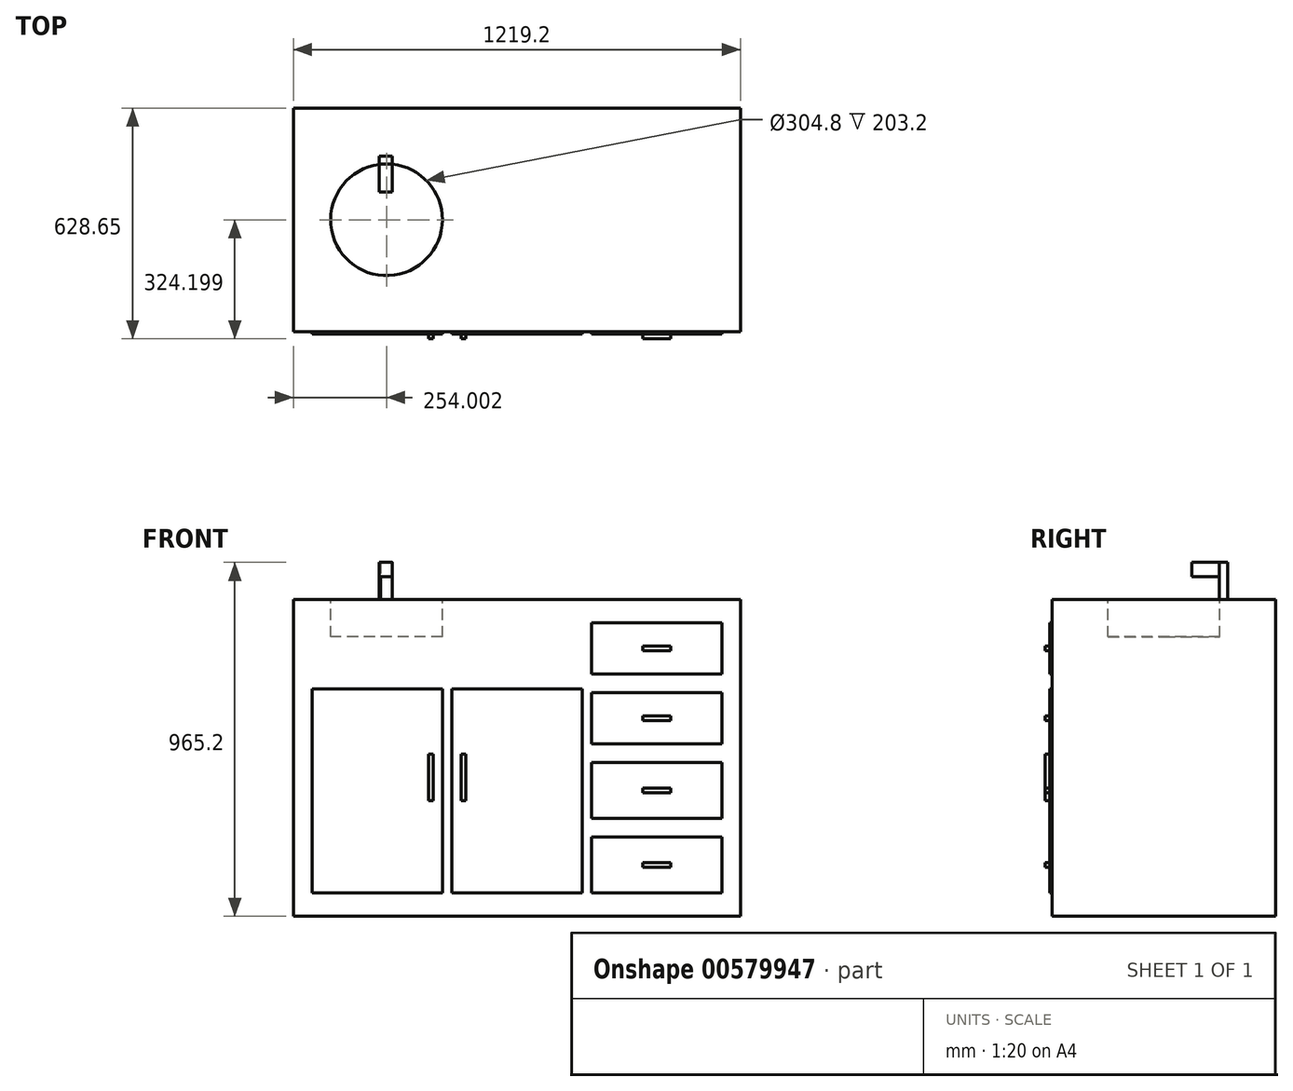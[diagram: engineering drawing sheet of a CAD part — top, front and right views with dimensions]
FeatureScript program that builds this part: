
annotation { "Feature Type Name" : "Feature", "Feature Type Description" : "" }
export const myFeature = defineFeature(function(context is Context, id is Id, definition is map)
    precondition{}
    {
        {
            var Q0;
            Q0=qCreatedBy(makeId("Top.planeOp"),FACE);
            var sketch = newSketch(context, id + "F0", { "sketchPlane" : qUnion([Q0])});
            skLineSegment(sketch, "E0.bottom", {"start": v(-528.54, 334.5) * mm, "end": v(690.66, 334.5) * mm});
            skLineSegment(sketch, "E0.top", {"start": v(-528.54, -275.1) * mm, "end": v(690.66, -275.1) * mm});
            skLineSegment(sketch, "E0.left", {"start": v(-528.54, 334.5) * mm, "end": v(-528.54, -275.1) * mm});
            skLineSegment(sketch, "E0.right", {"start": v(690.66, 334.5) * mm, "end": v(690.66, -275.1) * mm});
            skSolve(sketch);
        }
        {
            var Q0;
            Q0=makeQuery(id+"F0.imprint","IMPRINT",FACE,{"disambiguationData":[TD([[makeQuery(id+"F0.imprint","IMPRINT",EDGE,{"derivedFrom":sQuery(id+"F0.wireOp",EDGE,"E0.bottom")}),-1.0]])]});
            extrude(context, id + "F1", {"entities" : qUnion([Q0]), "depth" : 863.6 * mm, "offsetDistance" : 25.4 * mm});
        }
        {
            var Q0;
            Q0=makeQuery(id+"F1.opExtrude","SWEPT_FACE",FACE,{"disambiguationData":[OSD([sQuery(id+"F0.wireOp",EDGE,"E0.top")])]});
            var sketch = newSketch(context, id + "F2", { "sketchPlane" : qUnion([Q0])});
            skLineSegment(sketch, "E1.bottom", {"start": v(-477.74, 620.01) * mm, "end": v(-122.14, 620.01) * mm});
            skLineSegment(sketch, "E1.top", {"start": v(-477.74, 63.5) * mm, "end": v(-122.14, 63.5) * mm});
            skLineSegment(sketch, "E1.left", {"start": v(-477.74, 620.01) * mm, "end": v(-477.74, 63.5) * mm});
            skLineSegment(sketch, "E1.right", {"start": v(-96.74, 620.01) * mm, "end": v(-96.74, 63.5) * mm});
            skLineSegment(sketch, "E2.bottom", {"start": v(-96.74, 620.01) * mm, "end": v(258.86, 620.01) * mm});
            skLineSegment(sketch, "E2.top", {"start": v(-96.74, 63.5) * mm, "end": v(258.86, 63.5) * mm});
            skLineSegment(sketch, "E2.left", {"start": v(-122.14, 620.01) * mm, "end": v(-122.14, 63.5) * mm});
            skLineSegment(sketch, "E2.right", {"start": v(258.86, 620.01) * mm, "end": v(258.86, 63.5) * mm});
            skLineSegment(sketch, "E3.bottom", {"start": v(284.26, 609.6) * mm, "end": v(639.86, 609.6) * mm});
            skLineSegment(sketch, "E3.top", {"start": v(284.26, 469.9) * mm, "end": v(639.86, 469.9) * mm});
            skLineSegment(sketch, "E3.left", {"start": v(284.26, 609.6) * mm, "end": v(284.26, 469.9) * mm});
            skLineSegment(sketch, "E3.right", {"start": v(639.86, 609.6) * mm, "end": v(639.86, 469.9) * mm});
            skLineSegment(sketch, "E4.bottom", {"start": v(284.26, 419.1) * mm, "end": v(639.86, 419.1) * mm});
            skLineSegment(sketch, "E4.top", {"start": v(284.26, 266.7) * mm, "end": v(639.86, 266.7) * mm});
            skLineSegment(sketch, "E4.left", {"start": v(284.26, 419.1) * mm, "end": v(284.26, 266.7) * mm});
            skLineSegment(sketch, "E4.right", {"start": v(639.86, 419.1) * mm, "end": v(639.86, 266.7) * mm});
            skLineSegment(sketch, "E5.bottom", {"start": v(284.26, 63.5) * mm, "end": v(639.86, 63.5) * mm});
            skLineSegment(sketch, "E5.top", {"start": v(284.26, 215.9) * mm, "end": v(639.86, 215.9) * mm});
            skLineSegment(sketch, "E5.left", {"start": v(284.26, 63.5) * mm, "end": v(284.26, 215.9) * mm});
            skLineSegment(sketch, "E5.right", {"start": v(639.86, 63.5) * mm, "end": v(639.86, 215.9) * mm});
            skLineSegment(sketch, "E6.bottom", {"start": v(284.26, 800.1) * mm, "end": v(639.86, 800.1) * mm});
            skLineSegment(sketch, "E6.top", {"start": v(284.26, 660.4) * mm, "end": v(639.86, 660.4) * mm});
            skLineSegment(sketch, "E6.left", {"start": v(284.26, 800.1) * mm, "end": v(284.26, 660.4) * mm});
            skLineSegment(sketch, "E6.right", {"start": v(639.86, 800.1) * mm, "end": v(639.86, 660.4) * mm});
            skSolve(sketch);
        }
        {
            var Q0;
            Q0 = qSketchRegion(id + "F2", true);
            extrude(context, id + "F3", {"entities" : qUnion([Q0]), "operationType" : NewBodyOperationType.ADD, "depth" : 6.35 * mm, "offsetDistance" : 25.4 * mm});
        }
        {
            var Q0;
            Q0=makeQuery(id+"F3.opExtrude","CAP_FACE",FACE,{"disambiguationData":[OSD([sQuery(id+"F2.wireOp",EDGE,"E1.bottom"),sQuery(id+"F2.wireOp",EDGE,"E1.top"),sQuery(id+"F2.wireOp",EDGE,"E1.left"),sQuery(id+"F2.wireOp",EDGE,"E2.left")])],"isStart":false});
            var sketch = newSketch(context, id + "F4", { "sketchPlane" : qUnion([Q0])});
            skLineSegment(sketch, "E7.bottom", {"start": v(-160.24, 442.21) * mm, "end": v(-147.54, 442.21) * mm});
            skLineSegment(sketch, "E7.top", {"start": v(-160.24, 315.21) * mm, "end": v(-147.54, 315.21) * mm});
            skLineSegment(sketch, "E7.left", {"start": v(-160.24, 442.21) * mm, "end": v(-160.24, 315.21) * mm});
            skLineSegment(sketch, "E7.right", {"start": v(-147.54, 442.21) * mm, "end": v(-147.54, 315.21) * mm});
            skLineSegment(sketch, "E8.bottom", {"start": v(-71.34, 442.21) * mm, "end": v(-58.64, 442.21) * mm});
            skLineSegment(sketch, "E8.top", {"start": v(-71.34, 315.21) * mm, "end": v(-58.64, 315.21) * mm});
            skLineSegment(sketch, "E8.left", {"start": v(-71.34, 442.21) * mm, "end": v(-71.34, 315.21) * mm});
            skLineSegment(sketch, "E8.right", {"start": v(-58.64, 442.21) * mm, "end": v(-58.64, 315.21) * mm});
            skLineSegment(sketch, "E9.bottom", {"start": v(423.96, 736.6) * mm, "end": v(500.16, 736.6) * mm});
            skLineSegment(sketch, "E9.top", {"start": v(423.96, 723.9) * mm, "end": v(500.16, 723.9) * mm});
            skLineSegment(sketch, "E9.left", {"start": v(423.96, 736.6) * mm, "end": v(423.96, 723.9) * mm});
            skLineSegment(sketch, "E9.right", {"start": v(500.16, 736.6) * mm, "end": v(500.16, 723.9) * mm});
            skLineSegment(sketch, "E10.bottom", {"start": v(423.96, 546.1) * mm, "end": v(500.16, 546.1) * mm});
            skLineSegment(sketch, "E10.top", {"start": v(423.96, 533.4) * mm, "end": v(500.16, 533.4) * mm});
            skLineSegment(sketch, "E10.left", {"start": v(423.96, 546.1) * mm, "end": v(423.96, 533.4) * mm});
            skLineSegment(sketch, "E10.right", {"start": v(500.16, 546.1) * mm, "end": v(500.16, 533.4) * mm});
            skLineSegment(sketch, "E11.bottom", {"start": v(423.96, 349.25) * mm, "end": v(500.16, 349.25) * mm});
            skLineSegment(sketch, "E11.top", {"start": v(423.96, 336.55) * mm, "end": v(500.16, 336.55) * mm});
            skLineSegment(sketch, "E11.left", {"start": v(423.96, 349.25) * mm, "end": v(423.96, 336.55) * mm});
            skLineSegment(sketch, "E11.right", {"start": v(500.16, 349.25) * mm, "end": v(500.16, 336.55) * mm});
            skLineSegment(sketch, "E12.bottom", {"start": v(423.96, 146.05) * mm, "end": v(500.16, 146.05) * mm});
            skLineSegment(sketch, "E12.top", {"start": v(423.96, 133.35) * mm, "end": v(500.16, 133.35) * mm});
            skLineSegment(sketch, "E12.left", {"start": v(423.96, 146.05) * mm, "end": v(423.96, 133.35) * mm});
            skLineSegment(sketch, "E12.right", {"start": v(500.16, 146.05) * mm, "end": v(500.16, 133.35) * mm});
            skSolve(sketch);
        }
        {
            var Q0;
            Q0 = qSketchRegion(id + "F4", true);
            extrude(context, id + "F5", {"entities" : qUnion([Q0]), "operationType" : NewBodyOperationType.ADD, "depth" : 12.7 * mm, "offsetDistance" : 25.4 * mm});
        }
        {
            var Q0;
            Q0=makeQuery(id+"F1.opExtrude","CAP_FACE",FACE,{"disambiguationData":[OSD([sQuery(id+"F0.wireOp",EDGE,"E0.bottom"),sQuery(id+"F0.wireOp",EDGE,"E0.top"),sQuery(id+"F0.wireOp",EDGE,"E0.left"),sQuery(id+"F0.wireOp",EDGE,"E0.right")])],"isStart":false});
            var sketch = newSketch(context, id + "F6", { "sketchPlane" : qUnion([Q0])});
            skCircle(sketch, "E13", {"center": v(-274.54, 30.05) * mm, "radius": 152.4 * mm});
            skSolve(sketch);
        }
        {
            var Q0;
            Q0=makeQuery(id+"F6.imprint","IMPRINT",FACE,{"disambiguationData":[TD([[makeQuery(id+"F6.imprint","IMPRINT",EDGE,{"derivedFrom":sQuery(id+"F6.wireOp",EDGE,"E13")}),1.0]])]});
            extrude(context, id + "F7", {"entities" : qUnion([Q0]), "operationType" : NewBodyOperationType.REMOVE, "oppositeDirection" : true, "depth" : 101.6 * mm, "offsetDistance" : 25.4 * mm});
        }
        {
            var Q0;
            Q0=makeQuery(id+"F1.opExtrude","CAP_FACE",FACE,{"disambiguationData":[OSD([sQuery(id+"F0.wireOp",EDGE,"E0.bottom"),sQuery(id+"F0.wireOp",EDGE,"E0.top"),sQuery(id+"F0.wireOp",EDGE,"E0.left"),sQuery(id+"F0.wireOp",EDGE,"E0.right")])],"isStart":false});
            var sketch = newSketch(context, id + "F8", { "sketchPlane" : qUnion([Q0])});
            skLineSegment(sketch, "E14.bottom", {"start": v(-295.12, 203.31) * mm, "end": v(-258.59, 203.31) * mm});
            skLineSegment(sketch, "E14.top", {"start": v(-295.12, 181.61) * mm, "end": v(-258.59, 181.61) * mm});
            skLineSegment(sketch, "E14.left", {"start": v(-295.12, 203.31) * mm, "end": v(-295.12, 181.61) * mm});
            skLineSegment(sketch, "E14.right", {"start": v(-258.59, 203.31) * mm, "end": v(-258.59, 181.61) * mm});
            skSolve(sketch);
        }
        {
            var Q0;
            Q0=makeQuery(id+"F8.imprint","IMPRINT",FACE,{"disambiguationData":[TD([[makeQuery(id+"F8.imprint","IMPRINT",EDGE,{"derivedFrom":sQuery(id+"F8.wireOp",EDGE,"E14.bottom")}),-1.0]])]});
            extrude(context, id + "F9", {"entities" : qUnion([Q0]), "operationType" : NewBodyOperationType.ADD, "depth" : 101.6 * mm, "offsetDistance" : 25.4 * mm});
        }
        {
            var Q0;
            Q0=makeQuery(id+"F9.opExtrude","SWEPT_FACE",FACE,{"disambiguationData":[OSD([sQuery(id+"F8.wireOp",EDGE,"E14.top")])]});
            var sketch = newSketch(context, id + "F10", { "sketchPlane" : qUnion([Q0])});
            skLineSegment(sketch, "E15.bottom", {"start": v(-295.12, 965.2) * mm, "end": v(-258.88, 965.2) * mm});
            skLineSegment(sketch, "E15.top", {"start": v(-295.12, 926.4) * mm, "end": v(-258.88, 926.4) * mm});
            skLineSegment(sketch, "E15.left", {"start": v(-295.12, 965.2) * mm, "end": v(-295.12, 926.4) * mm});
            skLineSegment(sketch, "E15.right", {"start": v(-258.88, 965.2) * mm, "end": v(-258.88, 926.4) * mm});
            skSolve(sketch);
        }
        {
            var Q0;
            {var subQ0=sQuery(id+"F10.wireOp",EDGE,"E15.left");Q0=makeQuery(id+"F10.imprint","IMPRINT",FACE,{"disambiguationData":[TD([[makeQuery(id+"F10.imprint","IMPRINT",EDGE,{"derivedFrom":subQ0}),1.0]])]});}
            var Q1;
            {var subQ3=sQuery(id+"F10.wireOp",EDGE,"E15.right");Q1=makeQuery(id+"F10.imprint","IMPRINT",FACE,{"disambiguationData":[TD([[makeQuery(id+"F10.imprint","IMPRINT",EDGE,{"derivedFrom":subQ3}),-1.0]])]});}
            extrude(context, id + "F11", {"entities" : qUnion([Q0, Q1]), "operationType" : NewBodyOperationType.ADD, "depth" : 76.2 * mm, "offsetDistance" : 25.4 * mm});
        }
    });
